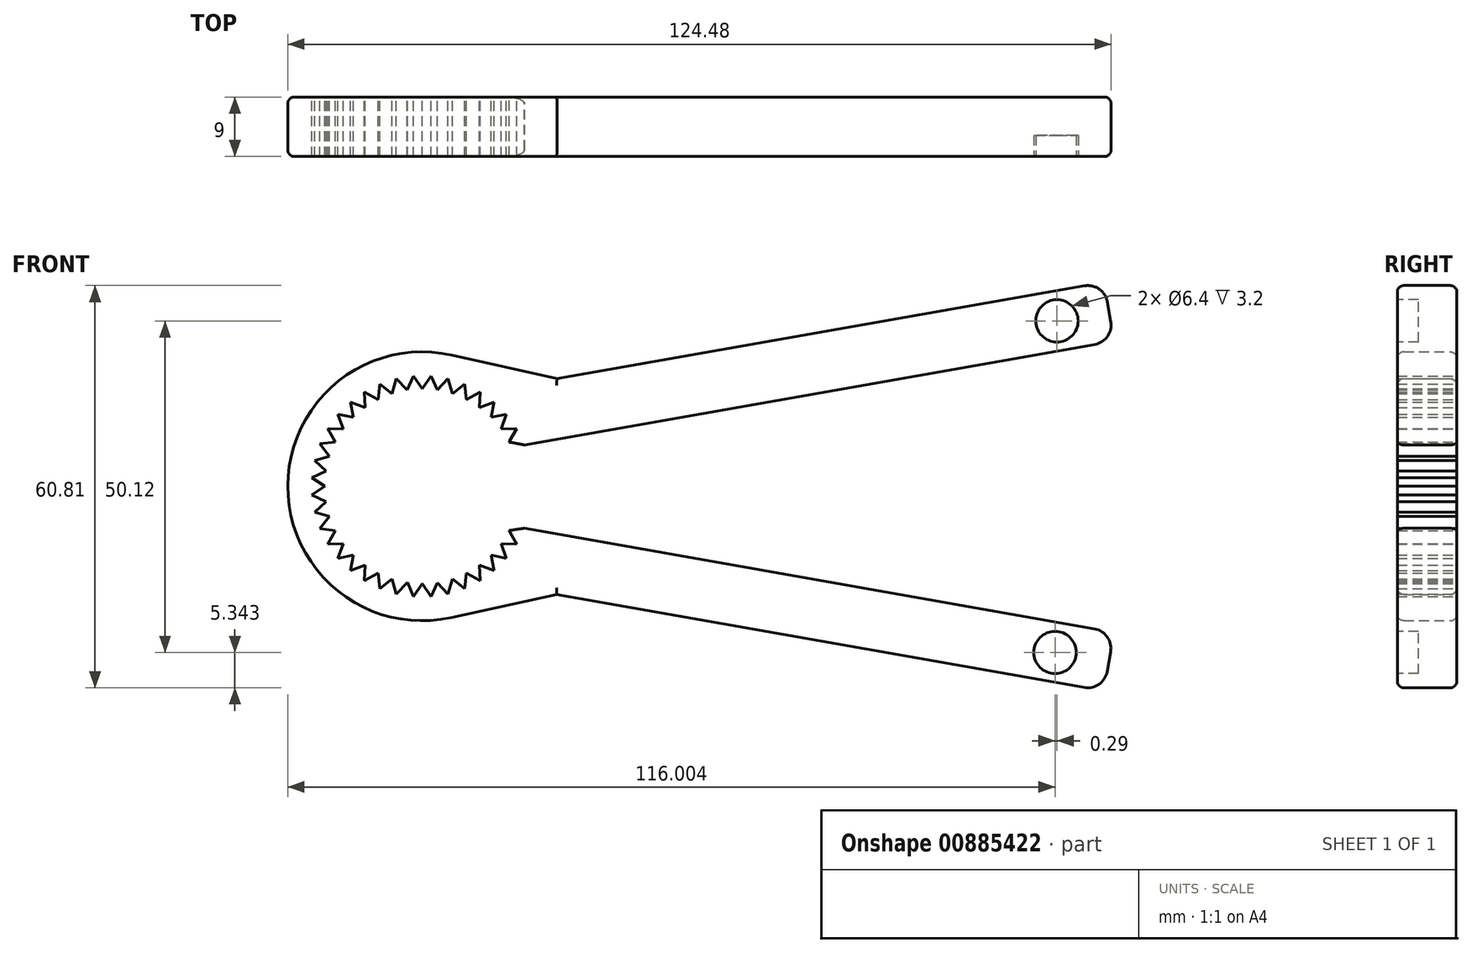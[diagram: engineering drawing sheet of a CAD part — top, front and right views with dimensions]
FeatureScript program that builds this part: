
annotation { "Feature Type Name" : "Feature", "Feature Type Description" : "" }
export const myFeature = defineFeature(function(context is Context, id is Id, definition is map)
    precondition{}
    {
        {
            var Q0;
            Q0=qCreatedBy(makeId("Front.planeOp"),FACE);
            var sketch = newSketch(context, id + "F0", { "sketchPlane" : qUnion([Q0])});
            skLineSegment(sketch, "E0", {"start": v(-21.5, 16.26) * mm, "end": v(58.24, 30.31) * mm});
            skLineSegment(sketch, "E1.0", {"start": v(-26.4, 6.26) * mm, "end": v(59.8, 21.45) * mm});
            skLineSegment(sketch, "E2", {"start": v(61.71, 27.88) * mm, "end": v(62.23, 24.92) * mm});
            skArc(sketch, "E3.filletArc", {"start": v(61.71, 27.88) * mm, "mid": v(60.48, 29.82) * mm, "end": v(58.24, 30.31) * mm});
            skArc(sketch, "E4.filletArc", {"start": v(59.8, 21.45) * mm, "mid": v(61.74, 22.68) * mm, "end": v(62.23, 24.92) * mm});
            skArc(sketch, "E5", {"start": v(-37.4, 19.84) * mm, "mid": v(-62.2, 0.06) * mm, "end": v(-37.51, -19.85) * mm});
            skPoint(sketch, "E5.first.point", {"position": v(-43.76, 20.25) * mm});
            skPoint(sketch, "E5.second.point", {"position": v(-40.6, -20.28) * mm});
            skPoint(sketch, "E5.third.point", {"position": v(-62.14, -1.59) * mm});
            skLineSegment(sketch, "E6", {"start": v(-175, 21.12) * mm, "end": v(-95.26, 35.17) * mm});
            skLineSegment(sketch, "E7.MirrorCS", {"start": v(-92.83, 38.64) * mm, "end": v(-93.35, 41.6) * mm});
            skArc(sketch, "E8.MirrorCS", {"start": v(-96.82, 44.03) * mm, "mid": v(-94.58, 43.54) * mm, "end": v(-93.35, 41.6) * mm});
            skArc(sketch, "E9.MirrorCS", {"start": v(-92.83, 38.64) * mm, "mid": v(-93.32, 36.4) * mm, "end": v(-95.26, 35.17) * mm});
            skLineSegment(sketch, "E10.MirrorCS", {"start": v(-183.58, 28.74) * mm, "end": v(-96.82, 44.03) * mm});
            skLineSegment(sketch, "E11", {"start": v(-21.54, -16.34) * mm, "end": v(58.2, -30.4) * mm});
            skLineSegment(sketch, "E12.MirrorCS", {"start": v(61.68, -27.97) * mm, "end": v(62.2, -25.02) * mm});
            skArc(sketch, "E13.MirrorCS", {"start": v(59.77, -21.54) * mm, "mid": v(61.7, -22.78) * mm, "end": v(62.2, -25.02) * mm});
            skArc(sketch, "E14.MirrorCS", {"start": v(61.68, -27.97) * mm, "mid": v(60.45, -29.91) * mm, "end": v(58.2, -30.4) * mm});
            skLineSegment(sketch, "E15.MirrorCS", {"start": v(-26.44, -6.33) * mm, "end": v(59.77, -21.54) * mm});
            skLineSegment(sketch, "E16", {"start": v(-21.5, 16.26) * mm, "end": v(-37.4, 19.84) * mm});
            skLineSegment(sketch, "E17", {"start": v(-21.54, -16.34) * mm, "end": v(-37.51, -19.85) * mm});
            skPoint(sketch, "E18.0.midPoint", {"position": v(-58.56, 0) * mm});
            skPoint(sketch, "E19.0.midPoint", {"position": v(-56.51, 1.16) * mm});
            skLineSegment(sketch, "E20", {"start": v(-54.6, 10.88) * mm, "end": v(-53.79, 8.67) * mm});
            skLineSegment(sketch, "E21", {"start": v(-53.79, 8.67) * mm, "end": v(-56.14, 8.75) * mm});
            skLineSegment(sketch, "E22", {"start": v(-56.14, 8.75) * mm, "end": v(-55, 6.7) * mm});
            skLineSegment(sketch, "E23", {"start": v(-55, 6.7) * mm, "end": v(-57.34, 6.41) * mm});
            skLineSegment(sketch, "E24", {"start": v(-57.34, 6.41) * mm, "end": v(-55.88, 4.56) * mm});
            skLineSegment(sketch, "E25", {"start": v(-55.88, 4.56) * mm, "end": v(-58.15, 3.92) * mm});
            skLineSegment(sketch, "E26", {"start": v(-58.15, 3.92) * mm, "end": v(-56.42, 2.31) * mm});
            skLineSegment(sketch, "E27", {"start": v(-56.42, 2.31) * mm, "end": v(-58.56, 1.32) * mm});
            skLineSegment(sketch, "E28", {"start": v(-58.56, 1.32) * mm, "end": v(-56.6, 0) * mm});
            skLineSegment(sketch, "E29", {"start": v(-56.6, 0) * mm, "end": v(-58.56, -1.3) * mm});
            skLineSegment(sketch, "E30", {"start": v(-58.56, -1.3) * mm, "end": v(-56.42, -2.3) * mm});
            skLineSegment(sketch, "E31", {"start": v(-56.42, -2.3) * mm, "end": v(-58.15, -3.9) * mm});
            skLineSegment(sketch, "E32", {"start": v(-58.15, -3.9) * mm, "end": v(-55.88, -4.54) * mm});
            skLineSegment(sketch, "E33", {"start": v(-55.88, -4.54) * mm, "end": v(-57.34, -6.4) * mm});
            skLineSegment(sketch, "E34", {"start": v(-57.34, -6.4) * mm, "end": v(-55, -6.68) * mm});
            skLineSegment(sketch, "E35", {"start": v(-55, -6.68) * mm, "end": v(-56.14, -8.74) * mm});
            skLineSegment(sketch, "E36", {"start": v(-56.14, -8.74) * mm, "end": v(-53.79, -8.65) * mm});
            skLineSegment(sketch, "E37", {"start": v(-53.79, -8.65) * mm, "end": v(-54.6, -10.86) * mm});
            skLineSegment(sketch, "E38", {"start": v(-54.6, -10.86) * mm, "end": v(-52.29, -10.4) * mm});
            skLineSegment(sketch, "E39", {"start": v(-52.29, -10.4) * mm, "end": v(-52.74, -12.72) * mm});
            skLineSegment(sketch, "E40", {"start": v(-50.62, -14.26) * mm, "end": v(-48.56, -13.12) * mm});
            skLineSegment(sketch, "E41", {"start": v(-48.28, -15.45) * mm, "end": v(-48.56, -13.12) * mm});
            skLineSegment(sketch, "E42", {"start": v(-50.53, -11.9) * mm, "end": v(-52.74, -12.72) * mm});
            skLineSegment(sketch, "E43", {"start": v(-50.62, -14.26) * mm, "end": v(-50.53, -11.9) * mm});
            skLineSegment(sketch, "E44", {"start": v(-48.28, -15.45) * mm, "end": v(-46.42, -14) * mm});
            skLineSegment(sketch, "E45", {"start": v(-44.1, -14.5) * mm, "end": v(-45.78, -16.27) * mm});
            skLineSegment(sketch, "E46", {"start": v(-46.42, -14) * mm, "end": v(-45.78, -16.27) * mm});
            skLineSegment(sketch, "E47", {"start": v(-44.1, -14.5) * mm, "end": v(-43.18, -16.68) * mm});
            skLineSegment(sketch, "E48", {"start": v(-43.18, -16.68) * mm, "end": v(-41.87, -14.72) * mm});
            skLineSegment(sketch, "E49", {"start": v(-41.87, -14.72) * mm, "end": v(-40.56, -16.68) * mm});
            skLineSegment(sketch, "E50", {"start": v(-40.56, -16.68) * mm, "end": v(-39.57, -14.54) * mm});
            skLineSegment(sketch, "E51", {"start": v(-39.57, -14.54) * mm, "end": v(-37.96, -16.27) * mm});
            skLineSegment(sketch, "E52", {"start": v(-37.96, -16.27) * mm, "end": v(-37.32, -14) * mm});
            skLineSegment(sketch, "E53", {"start": v(-37.32, -14) * mm, "end": v(-35.47, -15.45) * mm});
            skLineSegment(sketch, "E54", {"start": v(-35.47, -15.45) * mm, "end": v(-35.18, -13.12) * mm});
            skLineSegment(sketch, "E55", {"start": v(-35.18, -13.12) * mm, "end": v(-33.13, -14.26) * mm});
            skLineSegment(sketch, "E56", {"start": v(-33.13, -14.26) * mm, "end": v(-33.21, -11.9) * mm});
            skLineSegment(sketch, "E57", {"start": v(-33.21, -11.9) * mm, "end": v(-31, -12.72) * mm});
            skLineSegment(sketch, "E58", {"start": v(-31, -12.72) * mm, "end": v(-31.45, -10.4) * mm});
            skLineSegment(sketch, "E59", {"start": v(-31.45, -10.4) * mm, "end": v(-29.14, -10.86) * mm});
            skLineSegment(sketch, "E60", {"start": v(-29.95, -8.65) * mm, "end": v(-29.14, -10.86) * mm});
            skLineSegment(sketch, "E61", {"start": v(-27.6, -8.74) * mm, "end": v(-29.95, -8.65) * mm});
            skLineSegment(sketch, "E62", {"start": v(-27.6, -8.74) * mm, "end": v(-28.75, -6.68) * mm});
            skLineSegment(sketch, "E63", {"start": v(-28.75, -6.68) * mm, "end": v(-26.44, -6.33) * mm});
            skLineSegment(sketch, "E64", {"start": v(-26.4, 6.26) * mm, "end": v(-28.75, 6.7) * mm});
            skLineSegment(sketch, "E65", {"start": v(-28.75, 6.7) * mm, "end": v(-27.6, 8.75) * mm});
            skLineSegment(sketch, "E66", {"start": v(-27.6, 8.75) * mm, "end": v(-29.95, 8.67) * mm});
            skLineSegment(sketch, "E67", {"start": v(-29.95, 8.67) * mm, "end": v(-29.14, 10.88) * mm});
            skLineSegment(sketch, "E68", {"start": v(-29.14, 10.88) * mm, "end": v(-31.45, 10.43) * mm});
            skLineSegment(sketch, "E69", {"start": v(-31.45, 10.43) * mm, "end": v(-31, 12.74) * mm});
            skLineSegment(sketch, "E70", {"start": v(-31, 12.74) * mm, "end": v(-33.21, 11.93) * mm});
            skLineSegment(sketch, "E71", {"start": v(-33.21, 11.93) * mm, "end": v(-33.13, 14.28) * mm});
            skLineSegment(sketch, "E72", {"start": v(-33.13, 14.28) * mm, "end": v(-35.18, 13.14) * mm});
            skLineSegment(sketch, "E73", {"start": v(-35.18, 13.14) * mm, "end": v(-35.47, 15.47) * mm});
            skLineSegment(sketch, "E74", {"start": v(-35.47, 15.47) * mm, "end": v(-37.32, 14.02) * mm});
            skLineSegment(sketch, "E75", {"start": v(-37.32, 14.02) * mm, "end": v(-37.96, 16.28) * mm});
            skLineSegment(sketch, "E76", {"start": v(-37.96, 16.28) * mm, "end": v(-39.57, 14.56) * mm});
            skLineSegment(sketch, "E77", {"start": v(-39.57, 14.56) * mm, "end": v(-40.56, 16.7) * mm});
            skLineSegment(sketch, "E78", {"start": v(-40.56, 16.7) * mm, "end": v(-41.87, 14.74) * mm});
            skLineSegment(sketch, "E79", {"start": v(-41.87, 14.74) * mm, "end": v(-43.18, 16.7) * mm});
            skLineSegment(sketch, "E80", {"start": v(-43.18, 16.7) * mm, "end": v(-44.18, 14.56) * mm});
            skLineSegment(sketch, "E81", {"start": v(-44.18, 14.56) * mm, "end": v(-45.78, 16.28) * mm});
            skLineSegment(sketch, "E82", {"start": v(-45.78, 16.28) * mm, "end": v(-46.42, 14.02) * mm});
            skLineSegment(sketch, "E83", {"start": v(-46.42, 14.02) * mm, "end": v(-48.28, 15.47) * mm});
            skLineSegment(sketch, "E84", {"start": v(-48.28, 15.47) * mm, "end": v(-48.56, 13.14) * mm});
            skLineSegment(sketch, "E85", {"start": v(-48.56, 13.14) * mm, "end": v(-50.62, 14.28) * mm});
            skLineSegment(sketch, "E86", {"start": v(-50.62, 14.28) * mm, "end": v(-50.53, 11.93) * mm});
            skLineSegment(sketch, "E87", {"start": v(-50.53, 11.93) * mm, "end": v(-52.74, 12.74) * mm});
            skLineSegment(sketch, "E88", {"start": v(-52.74, 12.74) * mm, "end": v(-52.29, 10.43) * mm});
            skLineSegment(sketch, "E89", {"start": v(-52.29, 10.43) * mm, "end": v(-54.6, 10.88) * mm});
            skSolve(sketch);
        }
        {
            var Q0;
            Q0=makeQuery(id+"F0.imprint","IMPRINT",FACE,{"disambiguationData":[TD([[makeQuery(id+"F0.imprint","IMPRINT",EDGE,{"derivedFrom":sQuery(id+"F0.wireOp",EDGE,"E0")}),-1.0]])]});
            extrude(context, id + "F1", {"entities" : qUnion([Q0]), "depth" : 9 * mm, "offsetDistance" : 25 * mm});
        }
        {
            var Q0;
            Q0=makeQuery(id+"F1.opExtrude","CAP_EDGE",EDGE,{"disambiguationData":[OSD([sQuery(id+"F0.wireOp",EDGE,"E11")])],"isStart":false});
            var Q1;
            Q1=makeQuery(id+"F1.opExtrude","CAP_EDGE",EDGE,{"disambiguationData":[OSD([sQuery(id+"F0.wireOp",EDGE,"E5")])],"isStart":false});
            var Q2;
            Q2=makeQuery(id+"F1.opExtrude","CAP_EDGE",EDGE,{"disambiguationData":[OSD([sQuery(id+"F0.wireOp",EDGE,"E0")])],"isStart":false});
            var Q3;
            Q3=makeQuery(id+"F1.opExtrude","CAP_EDGE",EDGE,{"disambiguationData":[OSD([sQuery(id+"F0.wireOp",EDGE,"E11")])],"isStart":true});
            var Q4;
            Q4=makeQuery(id+"F1.opExtrude","CAP_EDGE",EDGE,{"disambiguationData":[OSD([sQuery(id+"F0.wireOp",EDGE,"E0")])],"isStart":true});
            var Q5;
            Q5=makeQuery(id+"F1.opExtrude","CAP_EDGE",EDGE,{"disambiguationData":[OSD([sQuery(id+"F0.wireOp",EDGE,"E5")])],"isStart":true});
            fillet(context, id + "F2", {"entities" : qUnion([Q0, Q1, Q2, Q3, Q4, Q5]), "radius" : 1 * mm, "tangentPropagation" : true, "allowEdgeOverflow" : false});
        }
        {
            var Q0;
            Q0=makeQuery(id+"F1.opExtrude","CAP_FACE",FACE,{"disambiguationData":[OSD([sQuery(id+"F0.wireOp",EDGE,"E0"),sQuery(id+"F0.wireOp",EDGE,"E1.0"),sQuery(id+"F0.wireOp",EDGE,"E2"),sQuery(id+"F0.wireOp",EDGE,"E3.filletArc"),sQuery(id+"F0.wireOp",EDGE,"E4.filletArc"),sQuery(id+"F0.wireOp",EDGE,"E5"),sQuery(id+"F0.wireOp",EDGE,"E11"),sQuery(id+"F0.wireOp",EDGE,"E12.MirrorCS"),sQuery(id+"F0.wireOp",EDGE,"E13.MirrorCS"),sQuery(id+"F0.wireOp",EDGE,"E14.MirrorCS"),sQuery(id+"F0.wireOp",EDGE,"E15.MirrorCS"),sQuery(id+"F0.wireOp",EDGE,"E16"),sQuery(id+"F0.wireOp",EDGE,"E17"),sQuery(id+"F0.wireOp",EDGE,"E20"),sQuery(id+"F0.wireOp",EDGE,"E21"),sQuery(id+"F0.wireOp",EDGE,"E22"),sQuery(id+"F0.wireOp",EDGE,"E23"),sQuery(id+"F0.wireOp",EDGE,"E24"),sQuery(id+"F0.wireOp",EDGE,"E25"),sQuery(id+"F0.wireOp",EDGE,"E26"),sQuery(id+"F0.wireOp",EDGE,"E27"),sQuery(id+"F0.wireOp",EDGE,"E28"),sQuery(id+"F0.wireOp",EDGE,"E29"),sQuery(id+"F0.wireOp",EDGE,"E30"),sQuery(id+"F0.wireOp",EDGE,"E31"),sQuery(id+"F0.wireOp",EDGE,"E32"),sQuery(id+"F0.wireOp",EDGE,"E33"),sQuery(id+"F0.wireOp",EDGE,"E34"),sQuery(id+"F0.wireOp",EDGE,"E35"),sQuery(id+"F0.wireOp",EDGE,"E36"),sQuery(id+"F0.wireOp",EDGE,"E37"),sQuery(id+"F0.wireOp",EDGE,"E38"),sQuery(id+"F0.wireOp",EDGE,"E39"),sQuery(id+"F0.wireOp",EDGE,"E40"),sQuery(id+"F0.wireOp",EDGE,"E41"),sQuery(id+"F0.wireOp",EDGE,"E42"),sQuery(id+"F0.wireOp",EDGE,"E43"),sQuery(id+"F0.wireOp",EDGE,"E44"),sQuery(id+"F0.wireOp",EDGE,"E45"),sQuery(id+"F0.wireOp",EDGE,"E46"),sQuery(id+"F0.wireOp",EDGE,"E47"),sQuery(id+"F0.wireOp",EDGE,"E48"),sQuery(id+"F0.wireOp",EDGE,"E49"),sQuery(id+"F0.wireOp",EDGE,"E50"),sQuery(id+"F0.wireOp",EDGE,"E51"),sQuery(id+"F0.wireOp",EDGE,"E52"),sQuery(id+"F0.wireOp",EDGE,"E53"),sQuery(id+"F0.wireOp",EDGE,"E54"),sQuery(id+"F0.wireOp",EDGE,"E55"),sQuery(id+"F0.wireOp",EDGE,"E56"),sQuery(id+"F0.wireOp",EDGE,"E57"),sQuery(id+"F0.wireOp",EDGE,"E58"),sQuery(id+"F0.wireOp",EDGE,"E59"),sQuery(id+"F0.wireOp",EDGE,"E60"),sQuery(id+"F0.wireOp",EDGE,"E61"),sQuery(id+"F0.wireOp",EDGE,"E62"),sQuery(id+"F0.wireOp",EDGE,"E63"),sQuery(id+"F0.wireOp",EDGE,"E64"),sQuery(id+"F0.wireOp",EDGE,"E65"),sQuery(id+"F0.wireOp",EDGE,"E66"),sQuery(id+"F0.wireOp",EDGE,"E67"),sQuery(id+"F0.wireOp",EDGE,"E68"),sQuery(id+"F0.wireOp",EDGE,"E69"),sQuery(id+"F0.wireOp",EDGE,"E70"),sQuery(id+"F0.wireOp",EDGE,"E71"),sQuery(id+"F0.wireOp",EDGE,"E72"),sQuery(id+"F0.wireOp",EDGE,"E73"),sQuery(id+"F0.wireOp",EDGE,"E74"),sQuery(id+"F0.wireOp",EDGE,"E75"),sQuery(id+"F0.wireOp",EDGE,"E76"),sQuery(id+"F0.wireOp",EDGE,"E77"),sQuery(id+"F0.wireOp",EDGE,"E78"),sQuery(id+"F0.wireOp",EDGE,"E79"),sQuery(id+"F0.wireOp",EDGE,"E80"),sQuery(id+"F0.wireOp",EDGE,"E81"),sQuery(id+"F0.wireOp",EDGE,"E82"),sQuery(id+"F0.wireOp",EDGE,"E83"),sQuery(id+"F0.wireOp",EDGE,"E84"),sQuery(id+"F0.wireOp",EDGE,"E85"),sQuery(id+"F0.wireOp",EDGE,"E86"),sQuery(id+"F0.wireOp",EDGE,"E87"),sQuery(id+"F0.wireOp",EDGE,"E88"),sQuery(id+"F0.wireOp",EDGE,"E89")])],"isStart":false});
            var sketch = newSketch(context, id + "F3", { "sketchPlane" : qUnion([Q0])});
            skCircle(sketch, "E90", {"center": v(54.1, 25.01) * mm, "radius": 3.2 * mm});
            skCircle(sketch, "E91", {"center": v(53.8, -25.1) * mm, "radius": 3.2 * mm});
            skSolve(sketch);
        }
        {
            var Q0;
            Q0=makeQuery(id+"F3.imprint","IMPRINT",FACE,{"disambiguationData":[TD([[makeQuery(id+"F3.imprint","IMPRINT",EDGE,{"derivedFrom":sQuery(id+"F3.wireOp",EDGE,"E90")}),1.0]])]});
            var Q1;
            Q1=makeQuery(id+"F3.imprint","IMPRINT",FACE,{"disambiguationData":[TD([[makeQuery(id+"F3.imprint","IMPRINT",EDGE,{"derivedFrom":sQuery(id+"F3.wireOp",EDGE,"E91")}),1.0]])]});
            extrude(context, id + "F4", {"entities" : qUnion([Q0, Q1]), "operationType" : NewBodyOperationType.REMOVE, "oppositeDirection" : true, "depth" : 3.2 * mm, "offsetDistance" : 25 * mm});
        }
    });
